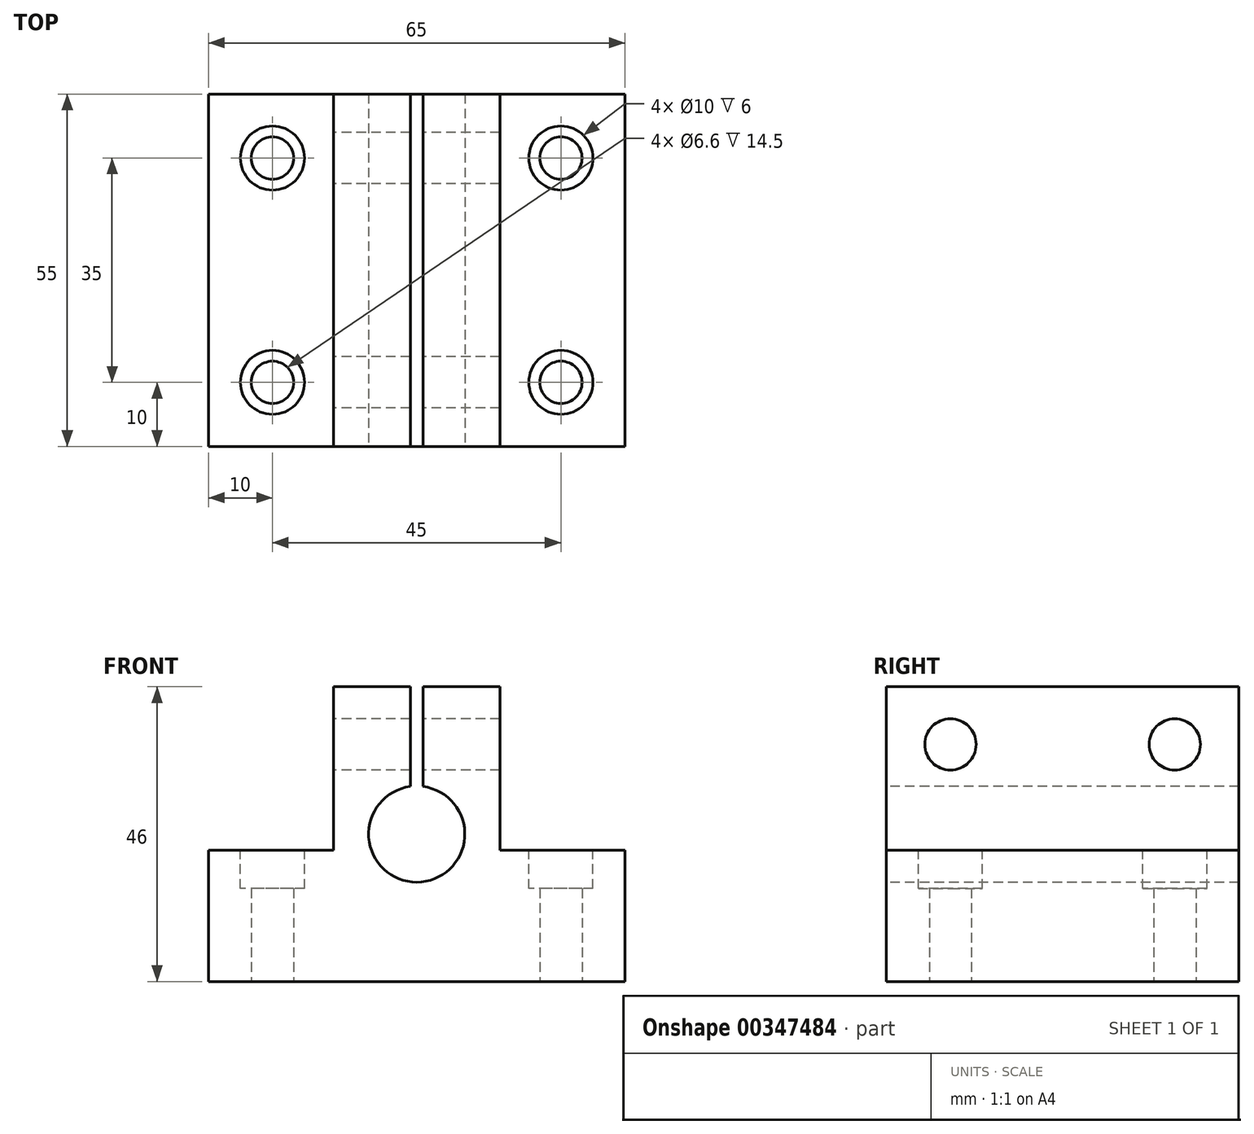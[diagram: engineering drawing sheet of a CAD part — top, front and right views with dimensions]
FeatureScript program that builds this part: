
annotation { "Feature Type Name" : "Feature", "Feature Type Description" : "" }
export const myFeature = defineFeature(function(context is Context, id is Id, definition is map)
    precondition{}
    {
        {
            var Q0;
            Q0=qCreatedBy(makeId("Top.planeOp"),FACE);
            var sketch = newSketch(context, id + "F0", { "sketchPlane" : qUnion([Q0])});
            skLineSegment(sketch, "E0.bottom", {"start": v(0, 0) * mm, "end": v(65, 0) * mm});
            skLineSegment(sketch, "E0.top", {"start": v(0, 55) * mm, "end": v(65, 55) * mm});
            skLineSegment(sketch, "E0.left", {"start": v(0, 0) * mm, "end": v(0, 55) * mm});
            skLineSegment(sketch, "E0.right", {"start": v(65, 0) * mm, "end": v(65, 55) * mm});
            skSolve(sketch);
        }
        {
            var Q0;
            Q0 = qSketchRegion(id + "F0", true);
            extrude(context, id + "F1", {"entities" : qUnion([Q0]), "depth" : 20.5 * mm});
        }
        {
            var Q0;
            Q0=makeQuery(id+"F1.opExtrude","CAP_FACE",FACE,{"disambiguationData":[OSD([sQuery(id+"F0.wireOp",EDGE,"E0.bottom"),sQuery(id+"F0.wireOp",EDGE,"E0.top"),sQuery(id+"F0.wireOp",EDGE,"E0.left"),sQuery(id+"F0.wireOp",EDGE,"E0.right")])],"isStart":false});
            var sketch = newSketch(context, id + "F2", { "sketchPlane" : qUnion([Q0])});
            skLineSegment(sketch, "E1", {"start": v(0, 0) * mm, "end": v(19.5, 0) * mm});
            skLineSegment(sketch, "E2", {"start": v(65, 0) * mm, "end": v(45.5, 0) * mm});
            skLineSegment(sketch, "E3", {"start": v(19.5, 0) * mm, "end": v(19.5, 55) * mm});
            skLineSegment(sketch, "E4", {"start": v(45.5, 0) * mm, "end": v(45.5, 55) * mm});
            skLineSegment(sketch, "E5", {"start": v(32.5, 0) * mm, "end": v(32.5, 55) * mm});
            skLineSegment(sketch, "E6", {"start": v(32.5, 0) * mm, "end": v(33.5, 0) * mm});
            skLineSegment(sketch, "E7", {"start": v(32.5, 0) * mm, "end": v(31.5, 0) * mm});
            skLineSegment(sketch, "E8", {"start": v(33.5, 0) * mm, "end": v(33.5, 55) * mm});
            skLineSegment(sketch, "E9", {"start": v(31.5, 0) * mm, "end": v(31.5, 55) * mm});
            skSolve(sketch);
        }
        {
            var Q0;
            Q0 = qSketchRegion(id + "F2", true);
            var Q1;
            {var subQ0=sQuery(id+"F2.wireOp",EDGE,"E3");Q1=makeQuery(id+"F2.imprint","IMPRINT",FACE,{"disambiguationData":[TD([[makeQuery(id+"F2.imprint","IMPRINT",EDGE,{"derivedFrom":subQ0}),-1.0]])]});}
            var Q2;
            {var subQ0=sQuery(id+"F2.wireOp",EDGE,"E4");Q2=makeQuery(id+"F2.imprint","IMPRINT",FACE,{"disambiguationData":[TD([[makeQuery(id+"F2.imprint","IMPRINT",EDGE,{"derivedFrom":subQ0}),1.0]])]});}
            extrude(context, id + "F3", {"entities" : qUnion([Q0, Q1, Q2]), "operationType" : NewBodyOperationType.ADD, "depth" : 25.5 * mm});
        }
        {
            var Q0;
            {var subQ0=sQuery(id+"F0.wireOp",EDGE,"E0.bottom");var subQ1=makeQuery(id+"F1.opExtrude","CAP_EDGE",EDGE,{"disambiguationData":[OSD([subQ0])],"isStart":false});Q0=makeQuery(id+"F3.boolean.opBoolean","MERGE",FACE,{"derivedFrom":[makeQuery(id+"F1.opExtrude","SWEPT_FACE",FACE,{"disambiguationData":[OSD([subQ0])]}),makeQuery(id+"F3.opExtrude","SWEPT_FACE",FACE,{"disambiguationData":[OSD([subQ0]),TDD([makeQuery(id+"F2.imprint","IMPRINT",EDGE,{"disambiguationData":[TD([[makeQuery(id+"F2.imprint","INTERSECT",VERTEX,{"derivedFrom":[subQ1,sQuery(id+"F2.wireOp",EDGE,"E1"),sQuery(id+"F2.wireOp",EDGE,"E3")]}),-1.0]])],"derivedFrom":subQ1})])]}),makeQuery(id+"F3.opExtrude","SWEPT_FACE",FACE,{"disambiguationData":[OSD([subQ0]),TDD([makeQuery(id+"F2.imprint","IMPRINT",EDGE,{"disambiguationData":[TD([[makeQuery(id+"F2.imprint","INTERSECT",VERTEX,{"derivedFrom":[subQ1,sQuery(id+"F2.wireOp",EDGE,"E2"),sQuery(id+"F2.wireOp",EDGE,"E4")]}),1.0]])],"derivedFrom":subQ1})])]})]});}
            var sketch = newSketch(context, id + "F4", { "sketchPlane" : qUnion([Q0])});
            skLineSegment(sketch, "E10", {"start": v(19.5, 46) * mm, "end": v(19.5, 23) * mm});
            skLineSegment(sketch, "E11", {"start": v(32.5, 20.5) * mm, "end": v(32.5, 29.43) * mm});
            skLineSegment(sketch, "E12", {"start": v(19.5, 23) * mm, "end": v(32.5, 23) * mm});
            skCircle(sketch, "E13", {"center": v(32.5, 23) * mm, "radius": 7.5 * mm});
            skSolve(sketch);
        }
        {
            var Q0;
            Q0 = qSketchRegion(id + "F4", true);
            extrude(context, id + "F5", {"entities" : qUnion([Q0]), "operationType" : NewBodyOperationType.REMOVE, "oppositeDirection" : true, "depth" : 74.8 * mm});
        }
        {
            var Q0;
            Q0=makeQuery(id+"F3.opExtrude","SWEPT_FACE",FACE,{"disambiguationData":[OSD([sQuery(id+"F2.wireOp",EDGE,"E3")])]});
            var sketch = newSketch(context, id + "F6", { "sketchPlane" : qUnion([Q0])});
            skLineSegment(sketch, "E14", {"start": v(-55, 46) * mm, "end": v(-45, 46) * mm});
            skLineSegment(sketch, "E15", {"start": v(-45, 46) * mm, "end": v(-45, 37) * mm});
            skLineSegment(sketch, "E16", {"start": v(0, 46) * mm, "end": v(-10, 46) * mm});
            skLineSegment(sketch, "E17", {"start": v(-10, 46) * mm, "end": v(-10, 37) * mm});
            skCircle(sketch, "E18", {"center": v(-45, 37) * mm, "radius": 4 * mm});
            skCircle(sketch, "E19", {"center": v(-10, 37) * mm, "radius": 4 * mm});
            skSolve(sketch);
        }
        {
            var Q0;
            Q0 = qSketchRegion(id + "F6", true);
            extrude(context, id + "F7", {"entities" : qUnion([Q0]), "operationType" : NewBodyOperationType.REMOVE, "oppositeDirection" : true, "depth" : 37.2 * mm});
        }
        {
            var Q0;
            Q0=makeQuery(id+"F1.opExtrude","CAP_FACE",FACE,{"disambiguationData":[OSD([sQuery(id+"F0.wireOp",EDGE,"E0.bottom"),sQuery(id+"F0.wireOp",EDGE,"E0.top"),sQuery(id+"F0.wireOp",EDGE,"E0.left"),sQuery(id+"F0.wireOp",EDGE,"E0.right")])],"isStart":true});
            var sketch = newSketch(context, id + "F8", { "sketchPlane" : qUnion([Q0])});
            skLineSegment(sketch, "E20", {"start": v(0, 0) * mm, "end": v(0, -10) * mm});
            skLineSegment(sketch, "E21", {"start": v(0, -10) * mm, "end": v(10, -10) * mm});
            skLineSegment(sketch, "E22", {"start": v(0, -55) * mm, "end": v(10, -55) * mm});
            skLineSegment(sketch, "E23", {"start": v(10, -55) * mm, "end": v(10, -45) * mm});
            skCircle(sketch, "E24", {"center": v(10, -45) * mm, "radius": 3.3 * mm});
            skCircle(sketch, "E25", {"center": v(10, -10) * mm, "radius": 3.3 * mm});
            skLineSegment(sketch, "E26", {"start": v(65, -55) * mm, "end": v(55, -55) * mm});
            skLineSegment(sketch, "E27", {"start": v(55, -55) * mm, "end": v(55, -45) * mm});
            skLineSegment(sketch, "E28", {"start": v(65, 0) * mm, "end": v(65, -10) * mm});
            skLineSegment(sketch, "E29", {"start": v(65, -10) * mm, "end": v(55, -10) * mm});
            skCircle(sketch, "E30", {"center": v(55, -45) * mm, "radius": 3.3 * mm});
            skCircle(sketch, "E31", {"center": v(55, -10) * mm, "radius": 3.3 * mm});
            skCircle(sketch, "E32", {"center": v(10, -45) * mm, "radius": 5 * mm});
            skCircle(sketch, "E33", {"center": v(10, -10) * mm, "radius": 5 * mm});
            skCircle(sketch, "E34", {"center": v(55, -45) * mm, "radius": 5 * mm});
            skCircle(sketch, "E35", {"center": v(55, -10) * mm, "radius": 5 * mm});
            skSolve(sketch);
        }
        {
            var Q0;
            Q0=makeQuery(id+"F2.imprint","IMPRINT",FACE,{"disambiguationData":[TD([[makeQuery(id+"F2.imprint","IMPRINT",EDGE,{"derivedFrom":sQuery(id+"F2.wireOp",EDGE,"E1")}),1.0]])]});
            var sketch = newSketch(context, id + "F9", { "sketchPlane" : qUnion([Q0])});
            skLineSegment(sketch, "E36", {"start": v(0, 0) * mm, "end": v(10, 0) * mm});
            skLineSegment(sketch, "E37", {"start": v(10, 0) * mm, "end": v(10, 10) * mm});
            skLineSegment(sketch, "E38", {"start": v(0, 0) * mm, "end": v(65, 0) * mm});
            skLineSegment(sketch, "E39", {"start": v(65, 0) * mm, "end": v(65, 10) * mm});
            skLineSegment(sketch, "E40", {"start": v(65, 10) * mm, "end": v(55, 10) * mm});
            skLineSegment(sketch, "E41", {"start": v(65, 0) * mm, "end": v(65, 55) * mm});
            skPoint(sketch, "E41.endSnap0", {"position": v(65, 5) * mm});
            skLineSegment(sketch, "E42", {"start": v(65, 55) * mm, "end": v(0, 55) * mm});
            skLineSegment(sketch, "E43", {"start": v(0, 55) * mm, "end": v(0, 45) * mm});
            skLineSegment(sketch, "E44", {"start": v(0, 45) * mm, "end": v(10, 45) * mm});
            skLineSegment(sketch, "E45", {"start": v(65, 55) * mm, "end": v(65, 45) * mm});
            skLineSegment(sketch, "E46", {"start": v(65, 45) * mm, "end": v(55, 45) * mm});
            skCircle(sketch, "E47", {"center": v(10, 45) * mm, "radius": 3.3 * mm});
            skCircle(sketch, "E48", {"center": v(10, 45) * mm, "radius": 5 * mm});
            skCircle(sketch, "E49", {"center": v(10, 10) * mm, "radius": 3.3 * mm});
            skCircle(sketch, "E50", {"center": v(10, 10) * mm, "radius": 5 * mm});
            skCircle(sketch, "E51", {"center": v(55, 10) * mm, "radius": 3.3 * mm});
            skCircle(sketch, "E52", {"center": v(55, 10) * mm, "radius": 5 * mm});
            skCircle(sketch, "E53", {"center": v(55, 45) * mm, "radius": 3.3 * mm});
            skCircle(sketch, "E54", {"center": v(55, 45) * mm, "radius": 5 * mm});
            skSolve(sketch);
        }
        {
            var Q0;
            Q0=makeQuery(id+"F9.imprint","IMPRINT",FACE,{"disambiguationData":[TD([[makeQuery(id+"F9.imprint","IMPRINT",EDGE,{"derivedFrom":sQuery(id+"F9.wireOp",EDGE,"E53")}),-1.0]])]});
            var Q1;
            Q1=makeQuery(id+"F9.imprint","IMPRINT",FACE,{"disambiguationData":[TD([[makeQuery(id+"F9.imprint","IMPRINT",EDGE,{"derivedFrom":sQuery(id+"F9.wireOp",EDGE,"E47")}),-1.0]])]});
            var Q2;
            Q2=makeQuery(id+"F9.imprint","IMPRINT",FACE,{"disambiguationData":[TD([[makeQuery(id+"F9.imprint","IMPRINT",EDGE,{"derivedFrom":sQuery(id+"F9.wireOp",EDGE,"E49")}),-1.0]])]});
            var Q3;
            Q3=makeQuery(id+"F9.imprint","IMPRINT",FACE,{"disambiguationData":[TD([[makeQuery(id+"F9.imprint","IMPRINT",EDGE,{"derivedFrom":sQuery(id+"F9.wireOp",EDGE,"E51")}),-1.0]])]});
            extrude(context, id + "F10", {"entities" : qUnion([Q0, Q1, Q2, Q3]), "operationType" : NewBodyOperationType.REMOVE, "oppositeDirection" : true, "depth" : 6 * mm});
        }
        {
            var Q0;
            Q0=makeQuery(id+"F8.imprint","IMPRINT",FACE,{"disambiguationData":[TD([[makeQuery(id+"F8.imprint","IMPRINT",EDGE,{"derivedFrom":sQuery(id+"F8.wireOp",EDGE,"E24")}),1.0]])]});
            var Q1;
            Q1=makeQuery(id+"F8.imprint","IMPRINT",FACE,{"disambiguationData":[TD([[makeQuery(id+"F8.imprint","IMPRINT",EDGE,{"derivedFrom":sQuery(id+"F8.wireOp",EDGE,"E30")}),1.0]])]});
            var Q2;
            Q2=makeQuery(id+"F8.imprint","IMPRINT",FACE,{"disambiguationData":[TD([[makeQuery(id+"F8.imprint","IMPRINT",EDGE,{"derivedFrom":sQuery(id+"F8.wireOp",EDGE,"E31")}),1.0]])]});
            var Q3;
            Q3=makeQuery(id+"F8.imprint","IMPRINT",FACE,{"disambiguationData":[TD([[makeQuery(id+"F8.imprint","IMPRINT",EDGE,{"derivedFrom":sQuery(id+"F8.wireOp",EDGE,"E25")}),1.0]])]});
            extrude(context, id + "F11", {"entities" : qUnion([Q0, Q1, Q2, Q3]), "operationType" : NewBodyOperationType.REMOVE, "oppositeDirection" : true, "depth" : 45.5 * mm});
        }
    });
